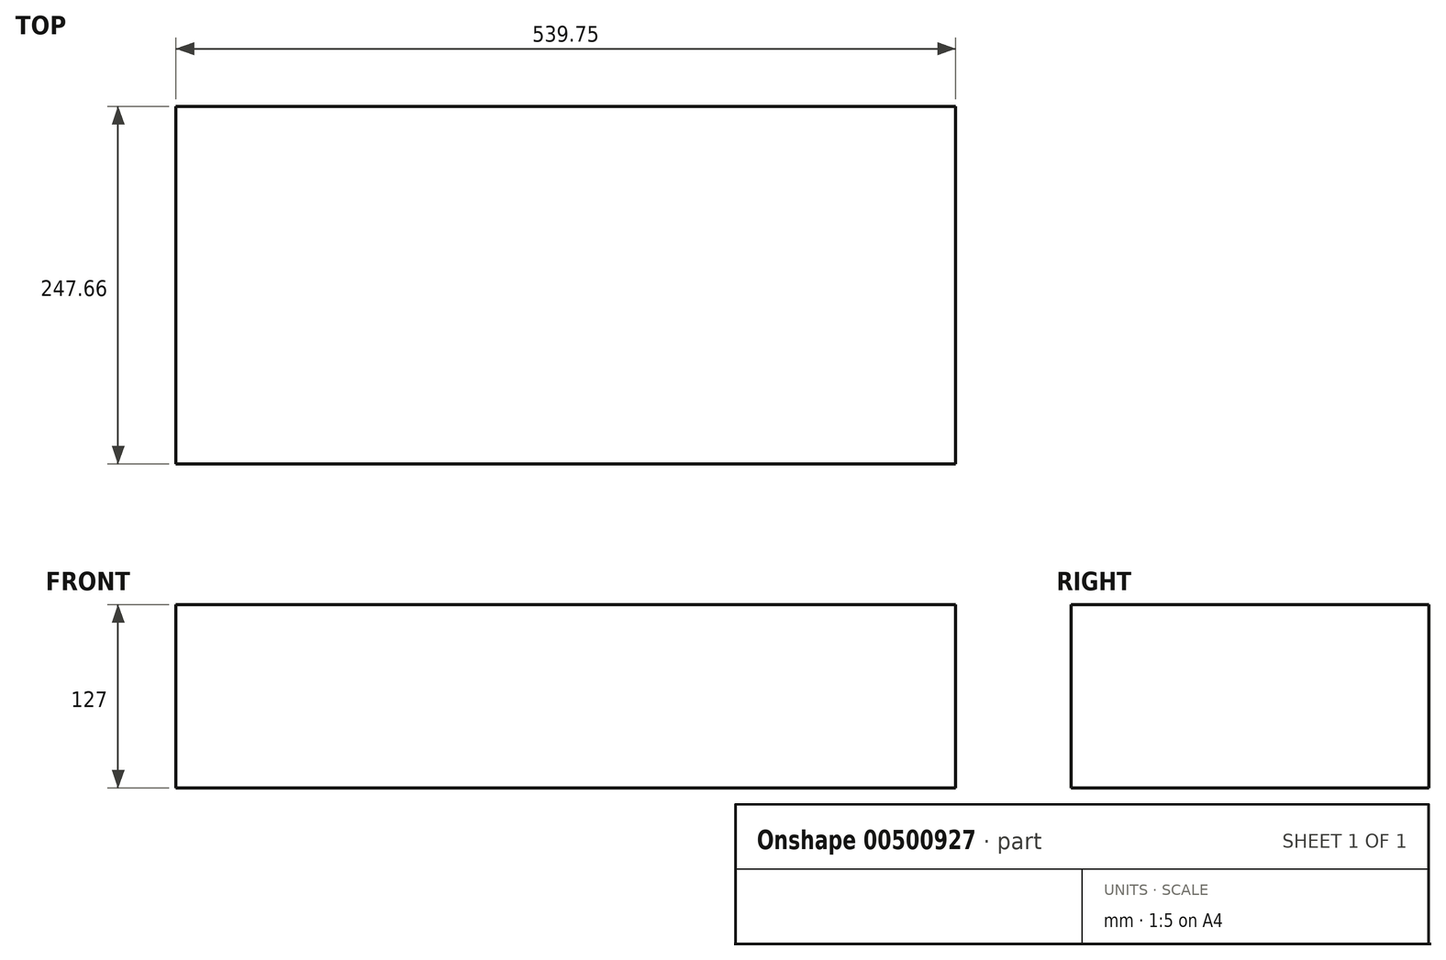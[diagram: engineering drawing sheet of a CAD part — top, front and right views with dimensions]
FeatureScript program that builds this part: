
annotation { "Feature Type Name" : "Feature", "Feature Type Description" : "" }
export const myFeature = defineFeature(function(context is Context, id is Id, definition is map)
    precondition{}
    {
        {
            var Q0;
            Q0=qCreatedBy(makeId("Top.planeOp"),FACE);
            var sketch = newSketch(context, id + "F0", { "sketchPlane" : qUnion([Q0])});
            skLineSegment(sketch, "E0.bottom", {"start": v(261.31, 123.82) * mm, "end": v(-278.44, 123.82) * mm});
            skLineSegment(sketch, "E0.top", {"start": v(261.31, -123.82) * mm, "end": v(-278.44, -123.82) * mm});
            skLineSegment(sketch, "E0.left", {"start": v(261.31, 123.82) * mm, "end": v(261.31, -123.82) * mm});
            skLineSegment(sketch, "E0.right", {"start": v(-278.44, 123.82) * mm, "end": v(-278.44, -123.82) * mm});
            skPoint(sketch, "E0.middle", {"position": v(-8.56, 0) * mm});
            skSolve(sketch);
        }
        {
            var Q0;
            Q0=makeQuery(id+"F0.imprint","IMPRINT",FACE,{"disambiguationData":[TD([[makeQuery(id+"F0.imprint","IMPRINT",EDGE,{"derivedFrom":sQuery(id+"F0.wireOp",EDGE,"E0.bottom")}),1.0]])]});
            extrude(context, id + "F1", {"entities" : qUnion([Q0]), "depth" : 127 * mm});
        }
    });
